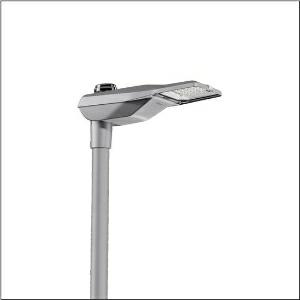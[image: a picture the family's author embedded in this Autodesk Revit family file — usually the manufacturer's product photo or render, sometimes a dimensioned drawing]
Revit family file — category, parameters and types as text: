
# Revit family: streetlight_sl_21_micro___p0_8a_5xe5u67n08db_bec5
name_source: partatom
category: Lighting Fixtures
units: mm (PartAtom-declared; Revit-internal decimal feet)

## family parameters
Cut with Voids When Loaded = No
Host = Face
Light Source = No
Part Type = Normal
Room Calculation Point = No
Round Connector Dimension = Use Diameter
Shared = No

## types (1)
- --- (1 x LED, 4520 lm, 39.1 W, 2700K)
    Apparent Load = 39 VA
    CIE Flux Codes = 33 69 96 100 100
    Color Rendering = 70
    Color Temperature = 2700K
    Default Elevation = 1800 mm
    Description = Streetlight SL 21 micro, mast luminaire, primary light control with lens, of PMMA, primary optical cover: cover, of toughened safety glass, transparent, light distribution: P0.8a, light emission: direct distribution, primary light characteristic: asymmetric, installation type: post-top, LED, 3G 1.5mm², High Power LED, rated luminous flux: 4.520lm, luminous efficacy: 116lm/W, light colour: 727, colour temperature: 2700K, control gear: NEMA (7pin), control: flexible luminous flux parameterisation, time-dependent luminous flux control, constant luminous flux control, pre-setting: linear dimming characteristic, overheat protection, mains connection: 230..240V, AC, 50/60Hz, connection cable pre-assembled, cable length: 6,5m, wiring characteristics: H07RN-F, start of lifetime: 39W, end of service life: 41W, reduction: 18W, luminaire housing, of diecast aluminium (EN AC-44300), powder-coated, SITECO metallic grey (DB 702S), corrosivity category C5 high according to DIN EN ISO 12944, multi-level sealing system, sealing non-destructively replaceable, inclination adjustable: 0°, 5°, 10°, 15°, length: 528mm, width: 235mm, height: 110mm, spigot size: 76/60mm (post-top), mounting height: 4..8m, protection rating (complete): IP66, insulation class (complete): insulation class I (protective earthing), certification: CE, ENEC, ENEC+, VDE, impact resistance: IK10, permissible operating ambient temperature for outdoor applications: -40..+50°C, standard-compliant lighting for roads and squares, packaging unit: 1 piece

Light Distribution: P0.8a
    Height = 110 mm
    Lamp = 1 x LED
    Lamp Light Flux = 4520 lm
    Lamp Power = 39.1 W
    Lamp count = 1
    Length = 528 mm
    Luminous efficacy = 116 lm/W
    Manufacturer = Siteco
    ModVariant = No
    Model = 5XE5U67N08DB
    Number of Poles = 1
    OnlyDefault = Yes
    Power Factor = 1
    Product Name = Streetlight SL 21 micro | P0.8a
    Product group = mast luminaire | pylon top
    ProductGroupID = 6100
    Protection Class = Protection class I
    Protection Degree = IP 66
    RLX_Detail_Level = 1
    RLX_Emergency_Light_Flux = 0 lm
    RLX_Emergency_Type = 0
    RLX_Emergency_Type_DB = No
    RlxData = <blob elided: 98789 chars, md5=60a2c6bd>
    Socket = socket
    Standby Power = 0 W
    System Light Flux = 4520 lm
    System Power = 39 W
    Type Comments = factory setting: luminous flux: 100 % | dim-lin: 254 | 765 mA
    Type Image = l_1294375.jpg
    URL = http://relux.com
    VarID = @adj_081401
    Voltage = 0 V
    Weight = 0.00 kg
    Width = 235 mm

## geometry (parser evidence)
native form markers: Blend x4, Sweep x11
no freeform markers — native parametric forms only
